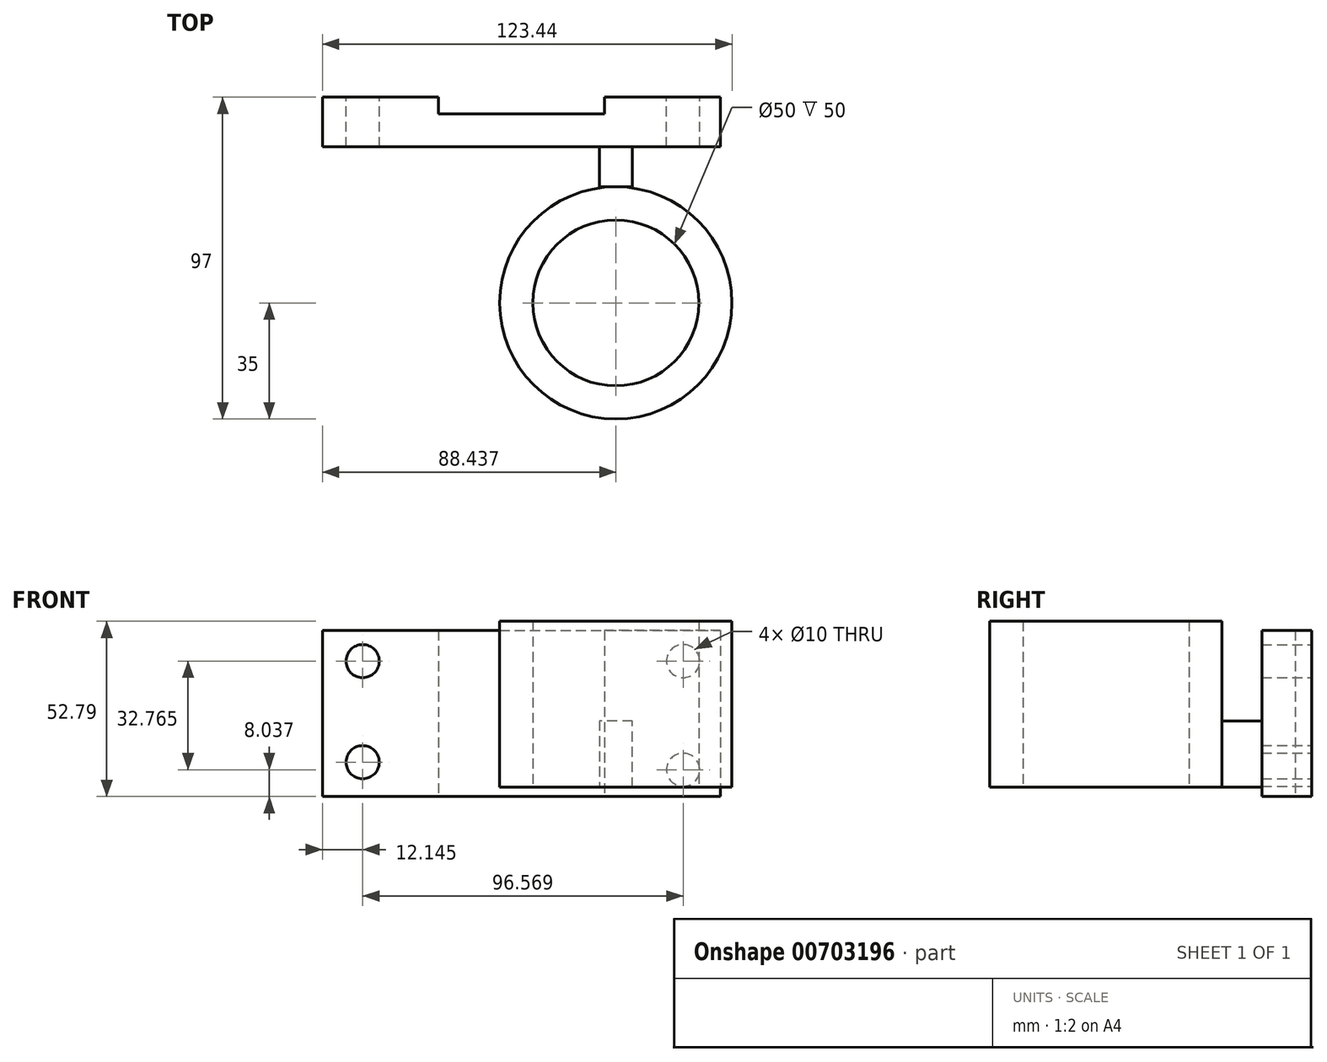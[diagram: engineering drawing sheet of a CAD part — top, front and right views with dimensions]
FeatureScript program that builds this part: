
annotation { "Feature Type Name" : "Feature", "Feature Type Description" : "" }
export const myFeature = defineFeature(function(context is Context, id is Id, definition is map)
    precondition{}
    {
        {
            var Q0;
            Q0=qCreatedBy(makeId("Front.planeOp"),FACE);
            var sketch = newSketch(context, id + "F0", { "sketchPlane" : qUnion([Q0])});
            skLineSegment(sketch, "E0", {"start": v(-56.55, -0.43) * mm, "end": v(63.45, -0.43) * mm});
            skLineSegment(sketch, "E1", {"start": v(63.45, -0.43) * mm, "end": v(63.45, -50.43) * mm});
            skLineSegment(sketch, "E2", {"start": v(63.45, -50.43) * mm, "end": v(-56.55, -50.43) * mm});
            skLineSegment(sketch, "E3", {"start": v(-56.55, -50.43) * mm, "end": v(-56.55, -0.43) * mm});
            skCircle(sketch, "E4", {"center": v(-44.4, -40.1) * mm, "radius": 5 * mm});
            skCircle(sketch, "E5", {"center": v(-44.4, -9.63) * mm, "radius": 5 * mm});
            skCircle(sketch, "E6", {"center": v(52.16, -9.63) * mm, "radius": 5 * mm});
            skCircle(sketch, "E7", {"center": v(52.16, -42.4) * mm, "radius": 5 * mm});
            skSolve(sketch);
        }
        {
            var Q0;
            Q0=makeQuery(id+"F0.imprint","IMPRINT",FACE,{"disambiguationData":[TD([[makeQuery(id+"F0.imprint","IMPRINT",EDGE,{"derivedFrom":sQuery(id+"F0.wireOp",EDGE,"E0")}),-1.0]])]});
            extrude(context, id + "F1", {"entities" : qUnion([Q0]), "depth" : 10 * mm, "offsetDistance" : 25 * mm});
        }
        {
            var Q0;
            Q0=makeQuery(id+"F1.opExtrude","SWEPT_FACE",FACE,{"disambiguationData":[OSD([sQuery(id+"F0.wireOp",EDGE,"E2")])]});
            var sketch = newSketch(context, id + "F2", { "sketchPlane" : qUnion([Q0])});
            skLineSegment(sketch, "E8", {"start": v(-56.55, 0) * mm, "end": v(-56.55, -5) * mm});
            skLineSegment(sketch, "E9", {"start": v(-56.55, -5) * mm, "end": v(-21.55, -5) * mm});
            skLineSegment(sketch, "E10", {"start": v(-21.55, -5) * mm, "end": v(-21.55, 0) * mm});
            skLineSegment(sketch, "E11", {"start": v(63.45, 0) * mm, "end": v(63.45, -5) * mm});
            skLineSegment(sketch, "E12", {"start": v(63.45, -5) * mm, "end": v(28.45, -5) * mm});
            skLineSegment(sketch, "E13", {"start": v(28.45, -5) * mm, "end": v(28.45, 0) * mm});
            skSolve(sketch);
        }
        {
            var Q0;
            {var subQ0=sQuery(id+"F2.wireOp",EDGE,"E8");Q0=makeQuery(id+"F2.imprint","IMPRINT",FACE,{"disambiguationData":[TD([[makeQuery(id+"F2.imprint","IMPRINT",EDGE,{"derivedFrom":subQ0}),1.0]])]});}
            var Q1;
            {var subQ0=sQuery(id+"F2.wireOp",EDGE,"E11");Q1=makeQuery(id+"F2.imprint","IMPRINT",FACE,{"disambiguationData":[TD([[makeQuery(id+"F2.imprint","IMPRINT",EDGE,{"derivedFrom":subQ0}),-1.0]])]});}
            extrude(context, id + "F3", {"entities" : qUnion([Q0, Q1]), "operationType" : NewBodyOperationType.ADD, "oppositeDirection" : true, "depth" : 50 * mm, "offsetDistance" : 25 * mm});
        }
        {
            var Q0;
            {var subQ0=sQuery(id+"F0.wireOp",EDGE,"E2");var subQ1=makeQuery(id+"F1.opExtrude","CAP_EDGE",EDGE,{"disambiguationData":[OSD([subQ0])],"isStart":true});Q0=makeQuery(id+"F3.boolean.opBoolean","SPLIT",FACE,{"disambiguationData":[TD([makeQuery(id+"F1.opExtrude","SWEPT_FACE",FACE,{"disambiguationData":[OSD([sQuery(id+"F0.wireOp",EDGE,"E5")])]})])],"derivedFrom":makeQuery(id+"F3.opExtrude","SWEPT_FACE",FACE,{"disambiguationData":[OSD([subQ0]),TDD([makeQuery(id+"F2.imprint","IMPRINT",EDGE,{"disambiguationData":[TD([[makeQuery(id+"F2.imprint","INTERSECT",VERTEX,{"derivedFrom":[subQ1,sQuery(id+"F2.wireOp",EDGE,"E10")]}),-1.0]])],"derivedFrom":subQ1})])]})});}
            var Q1;
            {var subQ0=sQuery(id+"F0.wireOp",EDGE,"E2");var subQ1=makeQuery(id+"F1.opExtrude","CAP_EDGE",EDGE,{"disambiguationData":[OSD([subQ0])],"isStart":true});Q1=makeQuery(id+"F3.boolean.opBoolean","SPLIT",FACE,{"disambiguationData":[TD([makeQuery(id+"F1.opExtrude","SWEPT_FACE",FACE,{"disambiguationData":[OSD([sQuery(id+"F0.wireOp",EDGE,"E4")])]})])],"derivedFrom":makeQuery(id+"F3.opExtrude","SWEPT_FACE",FACE,{"disambiguationData":[OSD([subQ0]),TDD([makeQuery(id+"F2.imprint","IMPRINT",EDGE,{"disambiguationData":[TD([[makeQuery(id+"F2.imprint","INTERSECT",VERTEX,{"derivedFrom":[subQ1,sQuery(id+"F2.wireOp",EDGE,"E10")]}),-1.0]])],"derivedFrom":subQ1})])]})});}
            var Q2;
            {var subQ0=sQuery(id+"F0.wireOp",EDGE,"E2");var subQ1=makeQuery(id+"F1.opExtrude","CAP_EDGE",EDGE,{"disambiguationData":[OSD([subQ0])],"isStart":true});Q2=makeQuery(id+"F3.boolean.opBoolean","SPLIT",FACE,{"disambiguationData":[TD([makeQuery(id+"F1.opExtrude","SWEPT_FACE",FACE,{"disambiguationData":[OSD([sQuery(id+"F0.wireOp",EDGE,"E6")])]})])],"derivedFrom":makeQuery(id+"F3.opExtrude","SWEPT_FACE",FACE,{"disambiguationData":[OSD([subQ0]),TDD([makeQuery(id+"F2.imprint","IMPRINT",EDGE,{"disambiguationData":[TD([[makeQuery(id+"F2.imprint","INTERSECT",VERTEX,{"derivedFrom":[subQ1,sQuery(id+"F2.wireOp",EDGE,"E13")]}),1.0]])],"derivedFrom":subQ1})])]})});}
            var Q3;
            {var subQ0=sQuery(id+"F0.wireOp",EDGE,"E2");var subQ1=makeQuery(id+"F1.opExtrude","CAP_EDGE",EDGE,{"disambiguationData":[OSD([subQ0])],"isStart":true});Q3=makeQuery(id+"F3.boolean.opBoolean","SPLIT",FACE,{"disambiguationData":[TD([makeQuery(id+"F1.opExtrude","SWEPT_FACE",FACE,{"disambiguationData":[OSD([sQuery(id+"F0.wireOp",EDGE,"E7")])]})])],"derivedFrom":makeQuery(id+"F3.opExtrude","SWEPT_FACE",FACE,{"disambiguationData":[OSD([subQ0]),TDD([makeQuery(id+"F2.imprint","IMPRINT",EDGE,{"disambiguationData":[TD([[makeQuery(id+"F2.imprint","INTERSECT",VERTEX,{"derivedFrom":[subQ1,sQuery(id+"F2.wireOp",EDGE,"E13")]}),1.0]])],"derivedFrom":subQ1})])]})});}
            extrude(context, id + "F4", {"entities" : qUnion([Q0, Q1, Q2, Q3]), "operationType" : NewBodyOperationType.REMOVE, "endBound" : BoundingType.THROUGH_ALL, "oppositeDirection" : true, "depth" : 25 * mm, "offsetDistance" : 25 * mm});
        }
        {
            var Q0;
            Q0=makeQuery(id+"F1.opExtrude","CAP_FACE",FACE,{"disambiguationData":[OSD([sQuery(id+"F0.wireOp",EDGE,"E0"),sQuery(id+"F0.wireOp",EDGE,"E1"),sQuery(id+"F0.wireOp",EDGE,"E2"),sQuery(id+"F0.wireOp",EDGE,"E3"),sQuery(id+"F0.wireOp",EDGE,"E4"),sQuery(id+"F0.wireOp",EDGE,"E5"),sQuery(id+"F0.wireOp",EDGE,"E6"),sQuery(id+"F0.wireOp",EDGE,"E7")])],"isStart":false});
            var sketch = newSketch(context, id + "F5", { "sketchPlane" : qUnion([Q0])});
            skLineSegment(sketch, "E14", {"start": v(36.89, -47.64) * mm, "end": v(36.89, -27.64) * mm});
            skLineSegment(sketch, "E15", {"start": v(36.89, -27.64) * mm, "end": v(26.89, -27.64) * mm});
            skLineSegment(sketch, "E16", {"start": v(26.89, -27.64) * mm, "end": v(26.89, -47.64) * mm});
            skLineSegment(sketch, "E17", {"start": v(26.89, -47.64) * mm, "end": v(26.89, -27.64) * mm});
            skLineSegment(sketch, "E18", {"start": v(36.89, -47.64) * mm, "end": v(26.89, -47.64) * mm});
            skSolve(sketch);
        }
        {
            var Q0;
            Q0 = qSketchRegion(id + "F5", true);
            extrude(context, id + "F6", {"entities" : qUnion([Q0]), "operationType" : NewBodyOperationType.ADD, "depth" : 12 * mm, "offsetDistance" : 25 * mm});
        }
        {
            var Q0;
            Q0=makeQuery(id+"F6.opExtrude","SWEPT_FACE",FACE,{"disambiguationData":[OSD([sQuery(id+"F5.wireOp",EDGE,"E18")])]});
            var sketch = newSketch(context, id + "F7", { "sketchPlane" : qUnion([Q0])});
            skCircle(sketch, "E19", {"center": v(31.89, 57) * mm, "radius": 35 * mm});
            skPoint(sketch, "E19.centerSnap0", {"position": v(31.89, 22) * mm});
            skCircle(sketch, "E20", {"center": v(31.89, 57) * mm, "radius": 25 * mm});
            skSolve(sketch);
        }
        {
            var Q0;
            Q0 = qSketchRegion(id + "F7", true);
            extrude(context, id + "F8", {"entities" : qUnion([Q0]), "operationType" : NewBodyOperationType.ADD, "oppositeDirection" : true, "depth" : 50 * mm, "offsetDistance" : 25 * mm});
        }
    });
